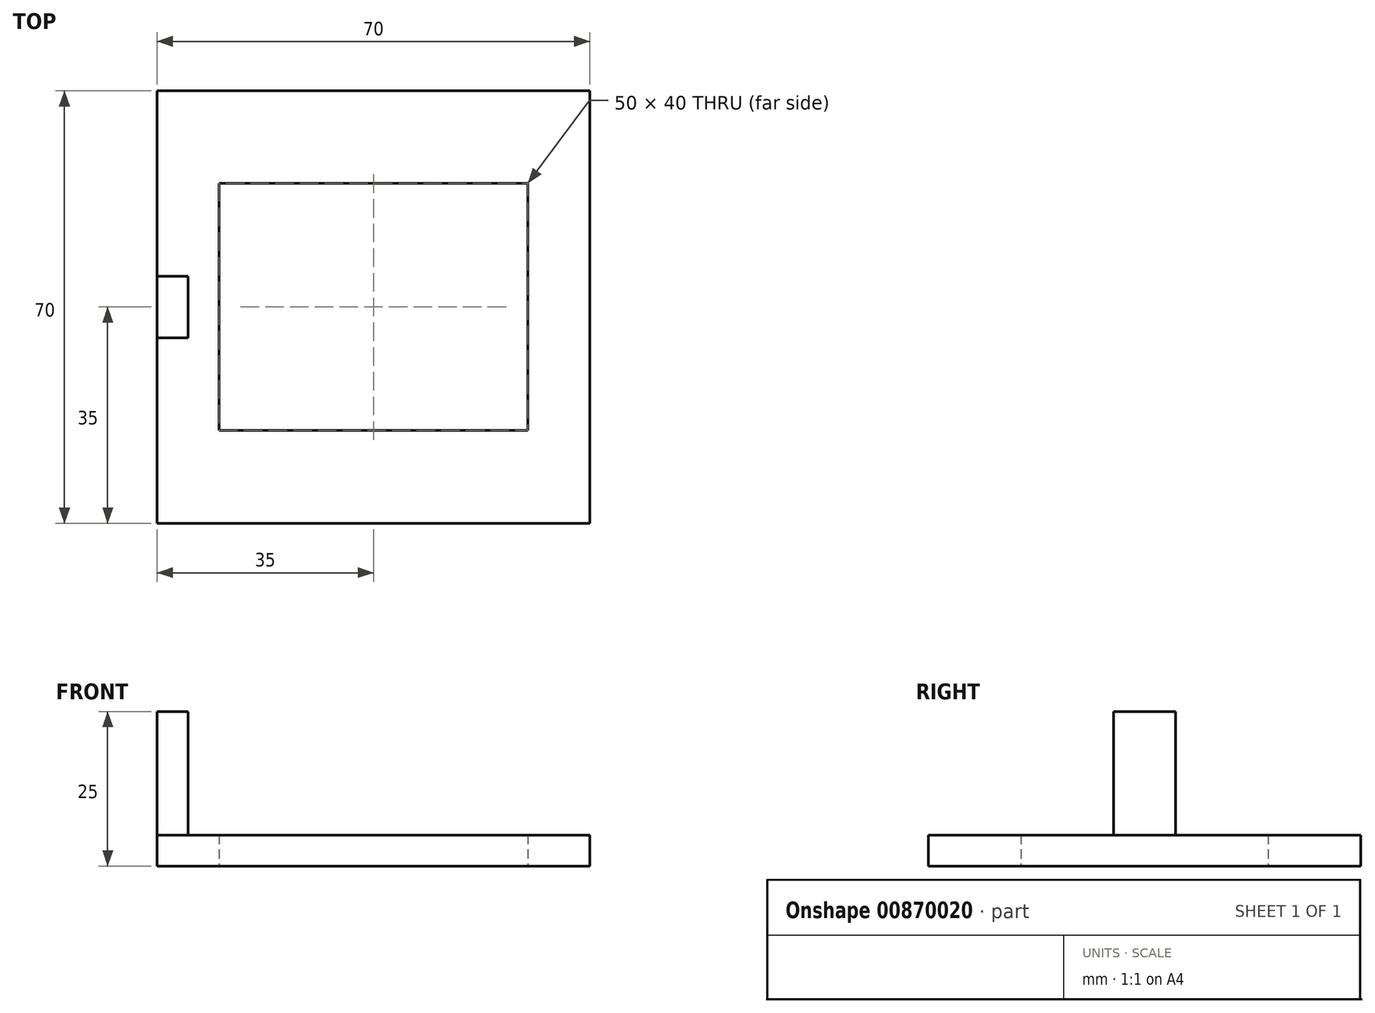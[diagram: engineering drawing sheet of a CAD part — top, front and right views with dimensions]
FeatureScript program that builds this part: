
annotation { "Feature Type Name" : "Feature", "Feature Type Description" : "" }
export const myFeature = defineFeature(function(context is Context, id is Id, definition is map)
    precondition{}
    {
        {
            var Q0;
            Q0=qCreatedBy(makeId("Top.planeOp"),FACE);
            var sketch = newSketch(context, id + "F0", { "sketchPlane" : qUnion([Q0])});
            skLineSegment(sketch, "E0.bottom", {"start": v(0, 0) * mm, "end": v(70, 0) * mm});
            skLineSegment(sketch, "E0.top", {"start": v(0, 70) * mm, "end": v(70, 70) * mm});
            skLineSegment(sketch, "E0.left", {"start": v(0, 0) * mm, "end": v(0, 70) * mm});
            skLineSegment(sketch, "E0.right", {"start": v(70, 0) * mm, "end": v(70, 70) * mm});
            skLineSegment(sketch, "E1.bottom", {"start": v(10, 55) * mm, "end": v(60, 55) * mm});
            skLineSegment(sketch, "E1.top", {"start": v(10, 15) * mm, "end": v(60, 15) * mm});
            skLineSegment(sketch, "E1.left", {"start": v(10, 55) * mm, "end": v(10, 15) * mm});
            skLineSegment(sketch, "E1.right", {"start": v(60, 55) * mm, "end": v(60, 15) * mm});
            skSolve(sketch);
        }
        {
            var Q0;
            Q0=makeQuery(id+"F0.imprint","IMPRINT",FACE,{"disambiguationData":[TD([[makeQuery(id+"F0.imprint","IMPRINT",EDGE,{"derivedFrom":sQuery(id+"F0.wireOp",EDGE,"E0.bottom")}),1.0]])]});
            var Q1;
            {var subQ0=sQuery(id+"F0.wireOp",EDGE,"sMfvxEbA-Ge8M-3Y2K-dLdj-D854MEGucAYe");Q1=makeQuery(id+"F0.imprint","IMPRINT",FACE,{"disambiguationData":[TD([[makeQuery(id+"F0.imprint","IMPRINT",EDGE,{"derivedFrom":subQ0}),-1.0]])]});}
            extrude(context, id + "F1", {"entities" : qUnion([Q0, Q1]), "depth" : 5 * mm, "offsetDistance" : 25 * mm});
        }
        {
            var Q0;
            Q0=qCreatedBy(makeId("Top.planeOp"),FACE);
            var sketch = newSketch(context, id + "F2", { "sketchPlane" : qUnion([Q0])});
            skLineSegment(sketch, "E2", {"start": v(0, 30) * mm, "end": v(5, 30) * mm});
            skLineSegment(sketch, "E3", {"start": v(5, 30) * mm, "end": v(5, 40) * mm});
            skLineSegment(sketch, "E4", {"start": v(5, 40) * mm, "end": v(0, 40) * mm});
            skLineSegment(sketch, "E5", {"start": v(0, 30) * mm, "end": v(0, 40) * mm});
            skSolve(sketch);
        }
        {
            var Q0;
            Q0=makeQuery(id+"F2.imprint","IMPRINT",FACE,{"disambiguationData":[TD([[makeQuery(id+"F2.imprint","IMPRINT",EDGE,{"derivedFrom":sQuery(id+"F2.wireOp",EDGE,"E2")}),1.0]])]});
            extrude(context, id + "F3", {"entities" : qUnion([Q0]), "operationType" : NewBodyOperationType.ADD, "depth" : 25 * mm, "offsetDistance" : 25 * mm});
        }
    });
